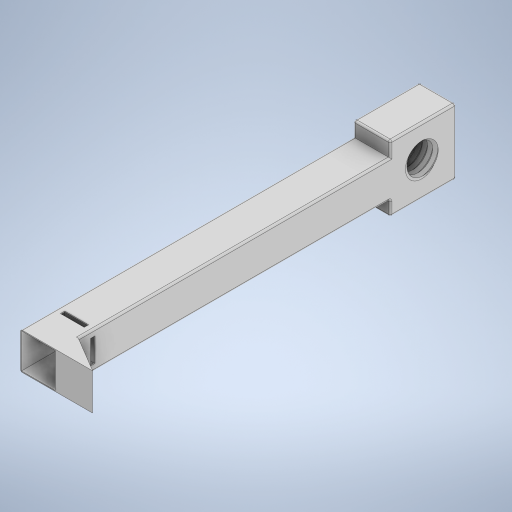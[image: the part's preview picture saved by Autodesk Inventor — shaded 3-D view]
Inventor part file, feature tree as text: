
AUTODESK INVENTOR PART (.ipt)
format: ipt  version: 2024 (Build 280153000, 153)  size: 514,560 bytes
history: native  units: mm
features: sketch x10, extrude x9, other x1, fillet x1
ambient origin geometry x8: Origin, YZ Plane, XZ Plane, XY Plane, X Axis, Y Axis, Z Axis, Center Point
bodies: Volumenkörper1 (feature_tree)
feature tree (21):
  extrude  "Extrusion1"  Depth=10.0mm
  extrude  "Extrusion2"  Depth=10.0mm
  extrude  "Extrusion3"  Depth=18.0mm TaperAngle=0.0deg
  extrude  "Extrusion4"  Depth=10.0mm TaperAngle=0.0deg
  other  "Spirale1"
  extrude  "Extrusion6"  Depth=9.0mm TaperAngle=0.0deg
  extrude  "Extrusion7"  Depth=10.0mm
  extrude  "Extrusion8"  Depth=0.2mm
  extrude  "Extrusion9"  Depth=9.5mm
  fillet  "Rundung2"  Radius=9.5mm
  extrude  "Extrusion10"  Depth=1.5mm
  sketch  "Skizze1"  dims[d0=10.0mm d1=10.0mm]
  sketch  "Skizze2"  dims[d2=91.0mm d3=0.0mm d4=10.0mm]
  sketch  "Skizze3"  dims[d5=18.0mm d6=18.0mm d7=0.0mm]
  sketch  "Skizze4"  dims[d8=10.0mm d9=9.0mm d10=0.0mm]
  sketch  "Skizze5"  dims[d17=7.2mm d18=9.0mm d19=0.0mm]
  sketch  "Skizze7"  dims[d22=1.4mm d23=11.0mm d24=10.0mm d25=0.0mm d26=90.0deg d27=90.0deg d28=0.0mm d29=0.0mm d33=1.7mm]
  sketch  "Skizze8"  dims[d34=60.0deg d35=0.2mm]
  sketch  "Skizze9"  dims[d36=1.0mm d37=0.0mm d39=9.5mm d40=9.5mm]
  sketch  "Skizze10"  dims[d41=9.75mm d42=0.0mm d43=1.5mm]
  sketch  "Skizze11"  dims[d44=1.5mm d45=0.5mm d46=0.5mm d47=1.5mm d48=1.5mm d49=1.5mm d50=1.5mm d51=0.5mm d52=0.5mm d53=1.2mm d54=0.0mm d55=2.0mm d56=0.0mm d57=0.5mm d59=0.5mm d60=10.0mm d61=0.0mm d38=0.0mm]
